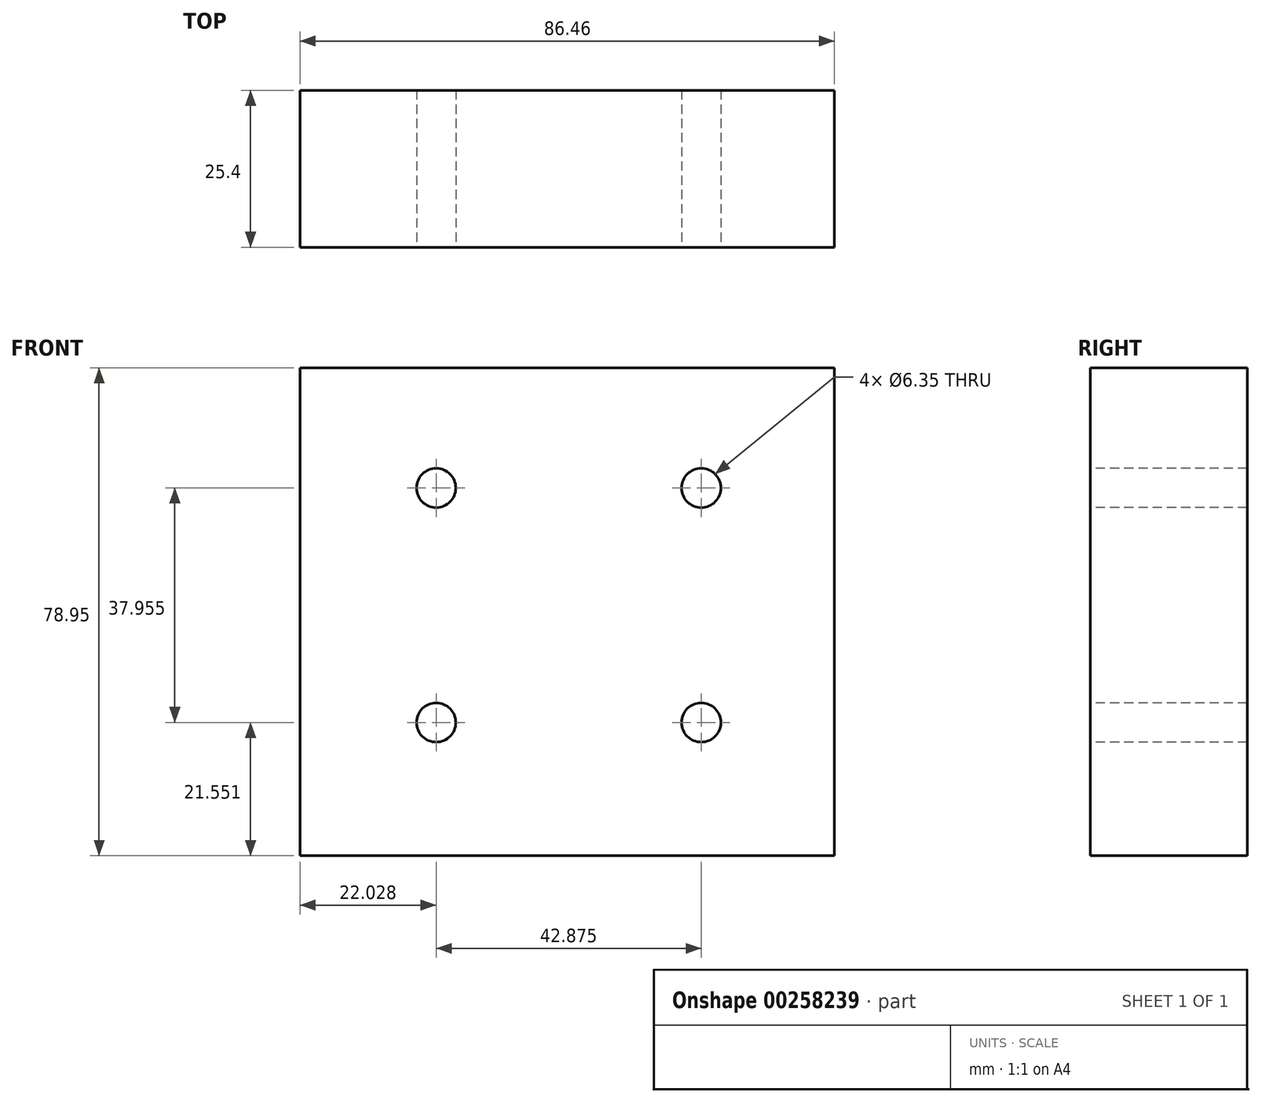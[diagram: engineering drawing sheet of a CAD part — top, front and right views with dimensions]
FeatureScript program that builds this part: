
annotation { "Feature Type Name" : "Feature", "Feature Type Description" : "" }
export const myFeature = defineFeature(function(context is Context, id is Id, definition is map)
    precondition{}
    {
        {
            var Q0;
            Q0=qCreatedBy(makeId("Front.planeOp"),FACE);
            var sketch = newSketch(context, id + "F0", { "sketchPlane" : qUnion([Q0])});
            skLineSegment(sketch, "E0.bottom", {"start": v(-44.52, 46.27) * mm, "end": v(41.94, 46.27) * mm});
            skLineSegment(sketch, "E0.top", {"start": v(-44.52, -32.68) * mm, "end": v(41.94, -32.68) * mm});
            skLineSegment(sketch, "E0.left", {"start": v(-44.52, 46.27) * mm, "end": v(-44.52, -32.68) * mm});
            skLineSegment(sketch, "E0.right", {"start": v(41.94, 46.27) * mm, "end": v(41.94, -32.68) * mm});
            skSolve(sketch);
        }
        {
            var Q0;
            Q0 = qSketchRegion(id + "F0", true);
            extrude(context, id + "F1", {"entities" : qUnion([Q0]), "depth" : 25.4 * mm});
        }
        {
            var Q0;
            Q0=makeQuery(id+"F1.opExtrude","CAP_FACE",FACE,{"disambiguationData":[OSD([sQuery(id+"F0.wireOp",EDGE,"E0.bottom"),sQuery(id+"F0.wireOp",EDGE,"E0.top"),sQuery(id+"F0.wireOp",EDGE,"E0.left"),sQuery(id+"F0.wireOp",EDGE,"E0.right")])],"isStart":false});
            var sketch = newSketch(context, id + "F2", { "sketchPlane" : qUnion([Q0])});
            skLineSegment(sketch, "E1.bottom", {"start": v(-22.5, 26.83) * mm, "end": v(20.38, 26.83) * mm});
            skLineSegment(sketch, "E1.top", {"start": v(-22.5, -11.13) * mm, "end": v(20.38, -11.13) * mm});
            skLineSegment(sketch, "E1.left", {"start": v(-22.5, 26.83) * mm, "end": v(-22.5, -11.13) * mm});
            skLineSegment(sketch, "E1.right", {"start": v(20.38, 26.83) * mm, "end": v(20.38, -11.13) * mm});
            skSolve(sketch);
        }
        {
            var Q0;
            Q0=sQuery(id+"F2.wireOp",VERTEX,"E1.left.start");
            var Q1;
            Q1=sQuery(id+"F2.wireOp",VERTEX,"E1.bottom.end");
            var Q2;
            Q2=sQuery(id+"F2.wireOp",VERTEX,"E1.top.end");
            var Q3;
            Q3=sQuery(id+"F2.wireOp",VERTEX,"E1.left.end");
            var Q4;
            Q4=makeQuery(id+"F1.opExtrude","SWEPT_BODY",BODY,{"disambiguationData":[OSD([sQuery(id+"F0.wireOp",EDGE,"E0.bottom"),sQuery(id+"F0.wireOp",EDGE,"E0.top"),sQuery(id+"F0.wireOp",EDGE,"E0.left"),sQuery(id+"F0.wireOp",EDGE,"E0.right")])]});
            hole(context, id + "F3", {"style" : HoleStyle.SIMPLE, "endStyle" : HoleEndStyle.THROUGH, "holeDiameter" : 6.35 * mm, "tappedDepth" : 12.7 * mm, "tapClearance" : 3, "locations" : qUnion([Q0, Q1, Q2, Q3]), "scope" : qUnion([Q4])});
        }
    });
